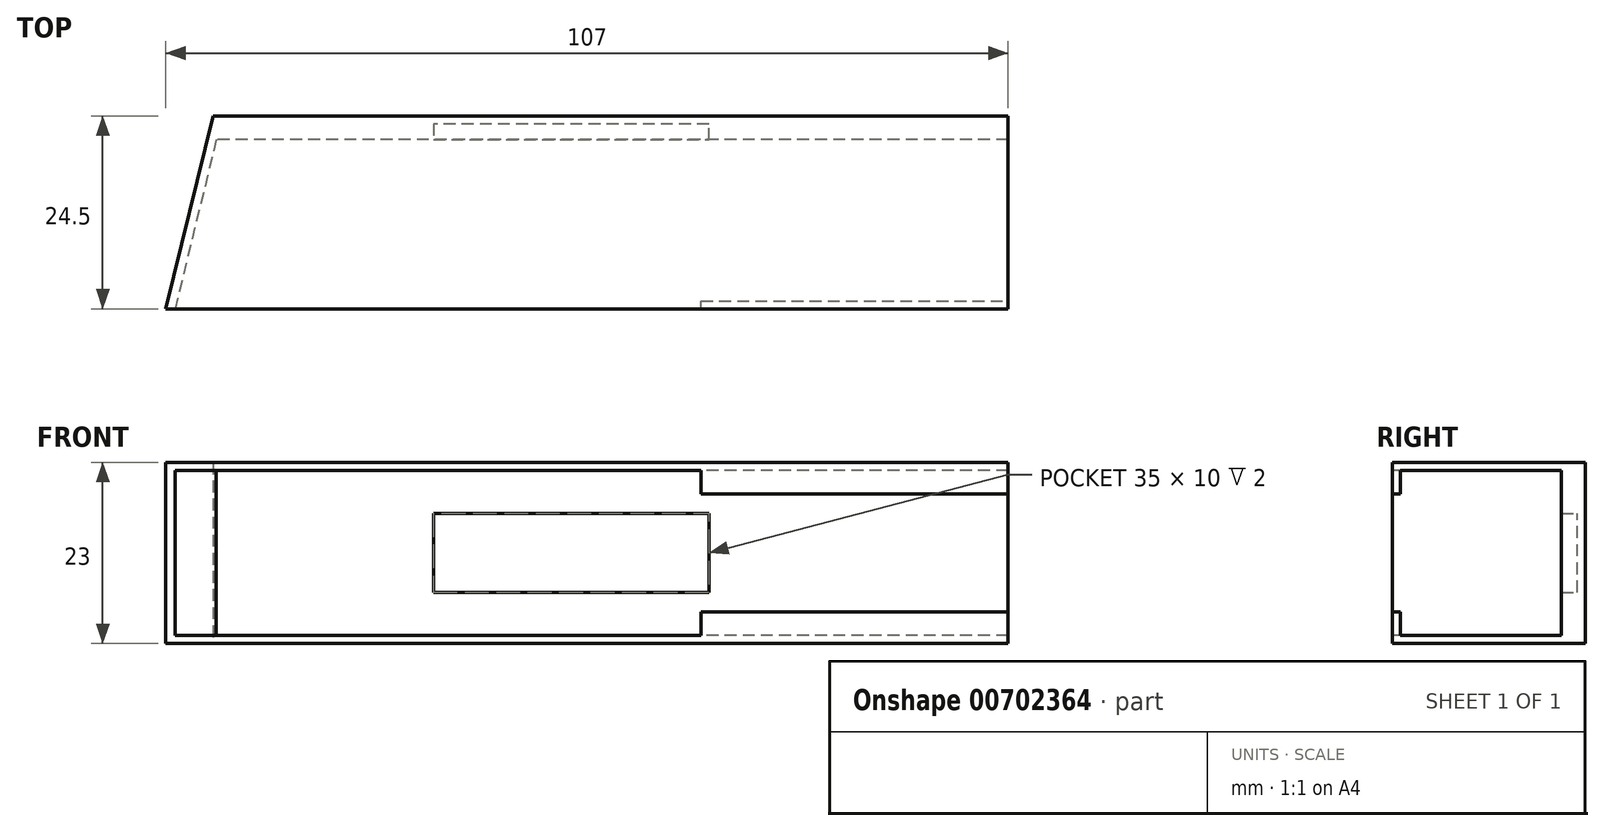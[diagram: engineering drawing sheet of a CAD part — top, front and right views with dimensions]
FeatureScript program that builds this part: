
annotation { "Feature Type Name" : "Feature", "Feature Type Description" : "" }
export const myFeature = defineFeature(function(context is Context, id is Id, definition is map)
    precondition{}
    {
        {
            var Q0;
            Q0=qCreatedBy(makeId("Top.planeOp"),FACE);
            var sketch = newSketch(context, id + "F0", { "sketchPlane" : qUnion([Q0])});
            skLineSegment(sketch, "E0", {"start": v(-48.33, 19.23) * mm, "end": v(52.67, 19.23) * mm});
            skLineSegment(sketch, "E1", {"start": v(52.67, 19.23) * mm, "end": v(52.67, -5.27) * mm});
            skLineSegment(sketch, "E2", {"start": v(52.67, -5.27) * mm, "end": v(-54.33, -5.27) * mm});
            skLineSegment(sketch, "E3", {"start": v(-54.33, -5.27) * mm, "end": v(-48.33, 19.23) * mm});
            skSolve(sketch);
        }
        {
            var Q0;
            Q0=makeQuery(id+"F0.imprint","IMPRINT",FACE,{"disambiguationData":[TD([[makeQuery(id+"F0.imprint","IMPRINT",EDGE,{"derivedFrom":sQuery(id+"F0.wireOp",EDGE,"E0")}),-1.0]])]});
            extrude(context, id + "F1", {"entities" : qUnion([Q0]), "endBound" : BoundingType.SYMMETRIC, "depth" : 23 * mm, "offsetDistance" : 25 * mm});
        }
        {
            var Q0;
            Q0=qCreatedBy(makeId("Top.planeOp"),FACE);
            var sketch = newSketch(context, id + "F2", { "sketchPlane" : qUnion([Q0])});
            skLineSegment(sketch, "E4", {"start": v(53.67, -4.27) * mm, "end": v(53.67, 16.23) * mm});
            skLineSegment(sketch, "E5", {"start": v(53.67, 16.23) * mm, "end": v(-47.9, 16.23) * mm});
            skLineSegment(sketch, "E6", {"start": v(13.67, -4.27) * mm, "end": v(13.67, -7.27) * mm});
            skLineSegment(sketch, "E7", {"start": v(13.67, -7.27) * mm, "end": v(-53.66, -7.27) * mm});
            skLineSegment(sketch, "E8", {"start": v(-47.9, 16.23) * mm, "end": v(-53.66, -7.27) * mm});
            skLineSegment(sketch, "E9", {"start": v(53.67, -4.27) * mm, "end": v(13.67, -4.27) * mm});
            skSolve(sketch);
        }
        {
            var Q0;
            Q0=makeQuery(id+"F2.imprint","IMPRINT",FACE,{"disambiguationData":[TD([[makeQuery(id+"F2.imprint","IMPRINT",EDGE,{"derivedFrom":sQuery(id+"F2.wireOp",EDGE,"E4")}),1.0]])]});
            extrude(context, id + "F3", {"entities" : qUnion([Q0]), "operationType" : NewBodyOperationType.REMOVE, "endBound" : BoundingType.SYMMETRIC, "oppositeDirection" : true, "depth" : 21 * mm, "offsetDistance" : 25 * mm});
        }
        {
            var Q0;
            Q0=qCreatedBy(makeId("Top.planeOp"),FACE);
            var sketch = newSketch(context, id + "F4", { "sketchPlane" : qUnion([Q0])});
            skLineSegment(sketch, "E10.bottom", {"start": v(4.08, 8.92) * mm, "end": v(62, 8.92) * mm});
            skLineSegment(sketch, "E10.top", {"start": v(4.08, -16.64) * mm, "end": v(62, -16.64) * mm});
            skLineSegment(sketch, "E10.left", {"start": v(4.08, 8.92) * mm, "end": v(4.08, -16.64) * mm});
            skLineSegment(sketch, "E10.right", {"start": v(62, 8.92) * mm, "end": v(62, -16.64) * mm});
            skSolve(sketch);
        }
        {
            var Q0;
            Q0=makeQuery(id+"F4.imprint","IMPRINT",FACE,{"disambiguationData":[TD([[makeQuery(id+"F4.imprint","IMPRINT",EDGE,{"derivedFrom":sQuery(id+"F4.wireOp",EDGE,"E10.bottom")}),-1.0]])]});
            extrude(context, id + "F5", {"entities" : qUnion([Q0]), "operationType" : NewBodyOperationType.REMOVE, "endBound" : BoundingType.SYMMETRIC, "oppositeDirection" : true, "depth" : 15 * mm, "offsetDistance" : 25 * mm});
        }
        {
            var Q0;
            Q0=qCreatedBy(makeId("Top.planeOp"),FACE);
            var sketch = newSketch(context, id + "F6", { "sketchPlane" : qUnion([Q0])});
            skLineSegment(sketch, "E11", {"start": v(14.67, 18.23) * mm, "end": v(-20.33, 18.23) * mm});
            skLineSegment(sketch, "E12", {"start": v(-20.33, 18.23) * mm, "end": v(-20.33, 12.25) * mm});
            skLineSegment(sketch, "E13", {"start": v(-20.33, 12.25) * mm, "end": v(14.67, 12.25) * mm});
            skLineSegment(sketch, "E14", {"start": v(14.67, 12.25) * mm, "end": v(14.67, 18.23) * mm});
            skSolve(sketch);
        }
        {
            var Q0;
            Q0=makeQuery(id+"F6.imprint","IMPRINT",FACE,{"disambiguationData":[TD([[makeQuery(id+"F6.imprint","IMPRINT",EDGE,{"derivedFrom":sQuery(id+"F6.wireOp",EDGE,"E11")}),1.0]])]});
            extrude(context, id + "F7", {"entities" : qUnion([Q0]), "operationType" : NewBodyOperationType.REMOVE, "endBound" : BoundingType.SYMMETRIC, "oppositeDirection" : true, "depth" : 10 * mm, "offsetDistance" : 25 * mm});
        }
    });
